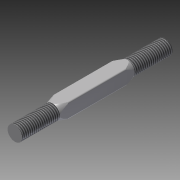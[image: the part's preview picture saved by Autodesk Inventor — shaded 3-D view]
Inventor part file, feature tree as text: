
AUTODESK INVENTOR PART (.ipt)
format: ipt  version: 2021 (Build 250183000, 183)  size: 150,528 bytes
history: native  units: mm
features: sketch x3, extrude x2, thread x2, other x1, plane x1, revolve x1, fillet x1
ambient origin geometry x8: Origin, YZ Plane, XZ Plane, XY Plane, X Axis, Y Axis, Z Axis, Center Point
bodies: Body1 (feature_tree)
feature tree (11):
  other  "Sólido1"
  extrude  "Extrusión1"  Depth=72.0mm TaperAngle=0.0deg
  plane  "Plano de trabajo1"
  extrude  "Extrusión3"  Depth=36.0mm TaperAngle=0.0deg
  revolve  "Revolución2"  [1 undecoded]
  fillet  "Empalme1"  Radius=7.0mm
  thread  "Rosca1"  [1 undecoded]
  thread  "Rosca2"  [1 undecoded]
  sketch  "Boceto1"  dims[d0=7.0mm d1=72.0mm d2=0.0mm]
  sketch  "Boceto3"  dims[d13=18.0mm d18=36.0mm d19=0.0mm]
  sketch  "Boceto4"  dims[d26=3.5mm d27=3.5mm d28=7.0mm d29=7.0mm d31=18.0mm d32=3.5mm d36=3.5mm d39=90.0deg d40=0.5mm d41=10.0mm d42=0.0mm d43=10.0mm d44=0.0mm]
note: 3 required parameter values undecoded (feature->parameter linkage not recoverable at this tier; creation-order binding heuristic only, values carry confidence <= 0.55)